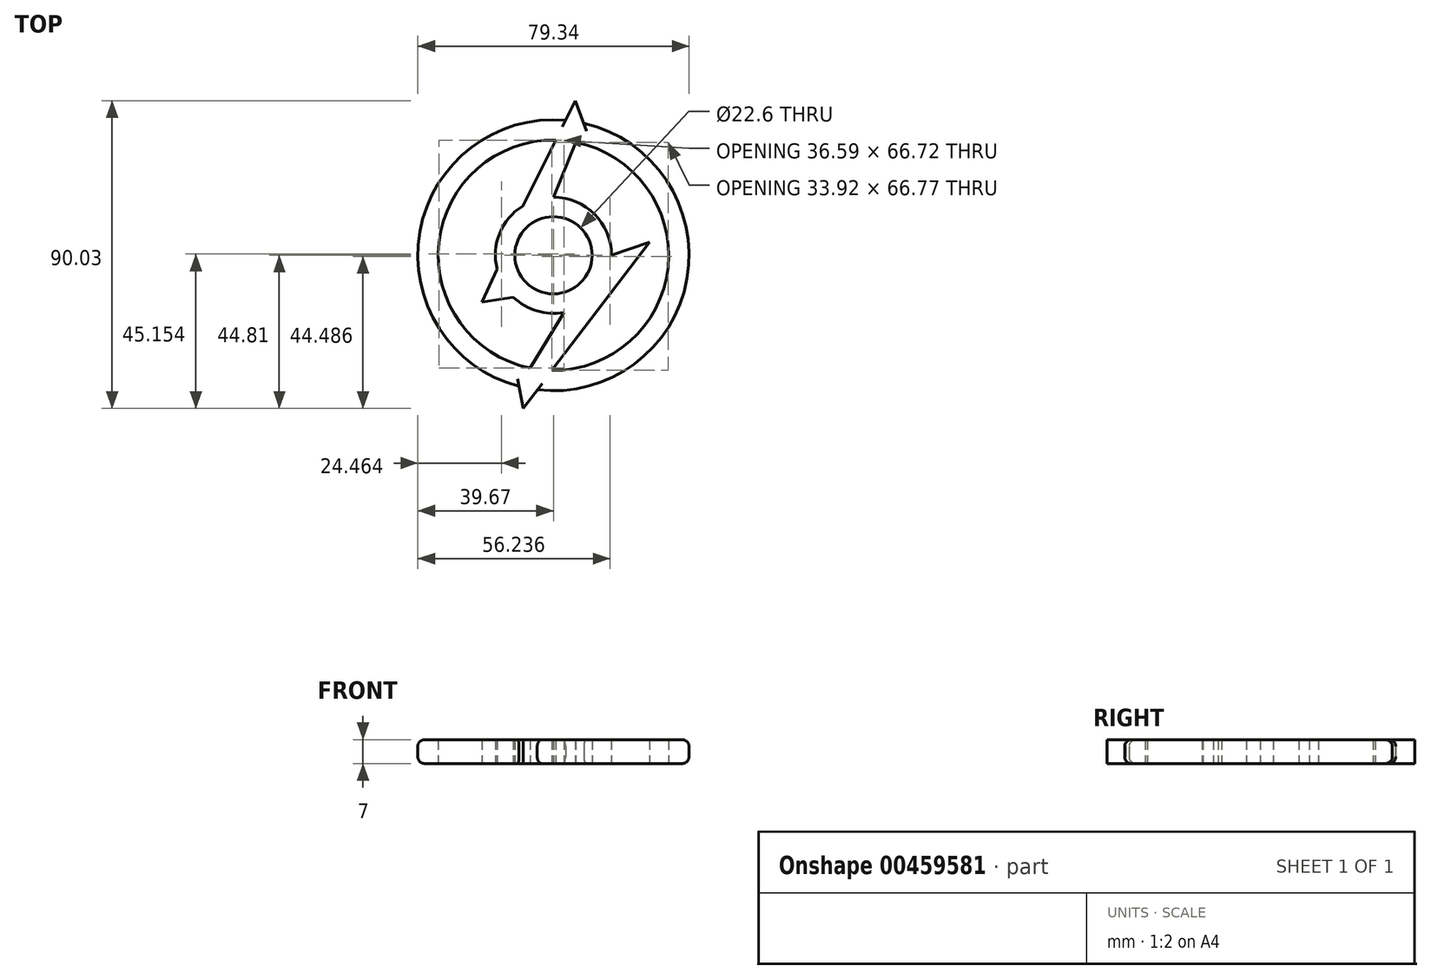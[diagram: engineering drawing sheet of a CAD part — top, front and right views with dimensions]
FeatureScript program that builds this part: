
annotation { "Feature Type Name" : "Feature", "Feature Type Description" : "" }
export const myFeature = defineFeature(function(context is Context, id is Id, definition is map)
    precondition{}
    {
        {
            var Q0;
            Q0=qCreatedBy(makeId("Top.planeOp"),FACE);
            var sketch = newSketch(context, id + "F0", { "sketchPlane" : qUnion([Q0])});
            skCircle(sketch, "E0", {"center": v(0, 0) * mm, "radius": 11.3 * mm});
            skCircle(sketch, "E1", {"center": v(0, 0) * mm, "radius": 16.98 * mm});
            skCircle(sketch, "E2", {"center": v(0, 0) * mm, "radius": 39.67 * mm});
            skCircle(sketch, "E3", {"center": v(0, 0) * mm, "radius": 33.7 * mm});
            skLineSegment(sketch, "E4", {"start": v(8.89, 38.67) * mm, "end": v(0, 16.98) * mm});
            skLineSegment(sketch, "E5", {"start": v(-8.85, -44.8) * mm, "end": v(-10.06, -38.38) * mm});
            skLineSegment(sketch, "E6", {"start": v(-10.06, -38.38) * mm, "end": v(3.09, -16.7) * mm});
            skLineSegment(sketch, "E7", {"start": v(-16.49, -4.06) * mm, "end": v(-20.96, -13.75) * mm});
            skLineSegment(sketch, "E8", {"start": v(-8.85, -44.8) * mm, "end": v(28.18, 3.8) * mm});
            skLineSegment(sketch, "E9", {"start": v(28.18, 3.8) * mm, "end": v(16.98, 0) * mm});
            skLineSegment(sketch, "E10", {"start": v(8.89, 38.67) * mm, "end": v(6.43, 45.22) * mm});
            skLineSegment(sketch, "E11", {"start": v(6.43, 45.22) * mm, "end": v(-9.01, 14.4) * mm});
            skLineSegment(sketch, "E12", {"start": v(-20.96, -13.75) * mm, "end": v(-11.71, -12.3) * mm});
            skSolve(sketch);
        }
        {
            var Q0;
            Q0 = qSketchRegion(id + "F0", true);
            var Q1;
            {var subQ0=sQuery(id+"F0.wireOp",EDGE,"E4");var subQ1=sQuery(id+"F0.wireOp",EDGE,"E1");var subQ2=makeQuery(id+"F0.imprint","INTERSECT",VERTEX,{"derivedFrom":[subQ1,subQ0]});Q1=makeQuery(id+"F0.imprint","IMPRINT",FACE,{"disambiguationData":[TD([[makeQuery(id+"F0.imprint","IMPRINT",EDGE,{"disambiguationData":[TD([[subQ2,-1.0]])],"derivedFrom":subQ1}),-1.0]])]});}
            var Q2;
            Q2=makeQuery(id+"F0.imprint","IMPRINT",FACE,{"disambiguationData":[TD([[makeQuery(id+"F0.imprint","IMPRINT",EDGE,{"derivedFrom":sQuery(id+"F0.wireOp",EDGE,"E0")}),-1.0]])]});
            var Q3;
            {var subQ0=sQuery(id+"F0.wireOp",EDGE,"E7");Q3=makeQuery(id+"F0.imprint","IMPRINT",FACE,{"disambiguationData":[TD([[makeQuery(id+"F0.imprint","IMPRINT",EDGE,{"derivedFrom":subQ0}),1.0]])]});}
            var Q4;
            {var subQ5=sQuery(id+"F0.wireOp",EDGE,"E9");Q4=makeQuery(id+"F0.imprint","IMPRINT",FACE,{"disambiguationData":[TD([[makeQuery(id+"F0.imprint","IMPRINT",EDGE,{"derivedFrom":subQ5}),1.0]])]});}
            extrude(context, id + "F1", {"entities" : qUnion([Q0, Q1, Q2, Q3, Q4]), "depth" : 7 * mm});
        }
        {
            var Q0;
            {var subQ0=sQuery(id+"F0.wireOp",EDGE,"E2");Q0=makeQuery(id+"F1.opExtrude","CAP_EDGE",EDGE,{"disambiguationData":[OSD([subQ0]),TDD([makeQuery(id+"F0.imprint","IMPRINT",EDGE,{"disambiguationData":[TD([[makeQuery(id+"F0.imprint","INTERSECT",VERTEX,{"derivedFrom":[subQ0,sQuery(id+"F0.wireOp",EDGE,"E8")]}),-1.0]])],"derivedFrom":subQ0})])],"isStart":false});}
            var Q1;
            {var subQ0=sQuery(id+"F0.wireOp",EDGE,"E2");Q1=makeQuery(id+"F1.opExtrude","CAP_EDGE",EDGE,{"disambiguationData":[OSD([subQ0]),TDD([makeQuery(id+"F0.imprint","IMPRINT",EDGE,{"disambiguationData":[TD([[makeQuery(id+"F0.imprint","INTERSECT",VERTEX,{"derivedFrom":[subQ0,sQuery(id+"F0.wireOp",EDGE,"E8")]}),-1.0]])],"derivedFrom":subQ0})])],"isStart":true});}
            var Q2;
            {var subQ0=sQuery(id+"F0.wireOp",EDGE,"E2");Q2=makeQuery(id+"F1.opExtrude","CAP_EDGE",EDGE,{"disambiguationData":[OSD([subQ0]),TDD([makeQuery(id+"F0.imprint","IMPRINT",EDGE,{"disambiguationData":[TD([[makeQuery(id+"F0.imprint","INTERSECT",VERTEX,{"derivedFrom":[subQ0,sQuery(id+"F0.wireOp",EDGE,"lKR6Do8w-2GbG-2u96-Iage-aeat0bwyVAHk")]}),-1.0]])],"derivedFrom":subQ0})])],"isStart":false});}
            var Q3;
            {var subQ0=sQuery(id+"F0.wireOp",EDGE,"E2");Q3=makeQuery(id+"F1.opExtrude","CAP_EDGE",EDGE,{"disambiguationData":[OSD([subQ0]),TDD([makeQuery(id+"F0.imprint","IMPRINT",EDGE,{"disambiguationData":[TD([[makeQuery(id+"F0.imprint","INTERSECT",VERTEX,{"derivedFrom":[subQ0,sQuery(id+"F0.wireOp",EDGE,"lKR6Do8w-2GbG-2u96-Iage-aeat0bwyVAHk")]}),-1.0]])],"derivedFrom":subQ0})])],"isStart":true});}
            fillet(context, id + "F2", {"entities" : qUnion([Q0, Q1, Q2, Q3]), "radius" : 2 * mm, "tangentPropagation" : true, "allowEdgeOverflow" : false});
        }
    });
